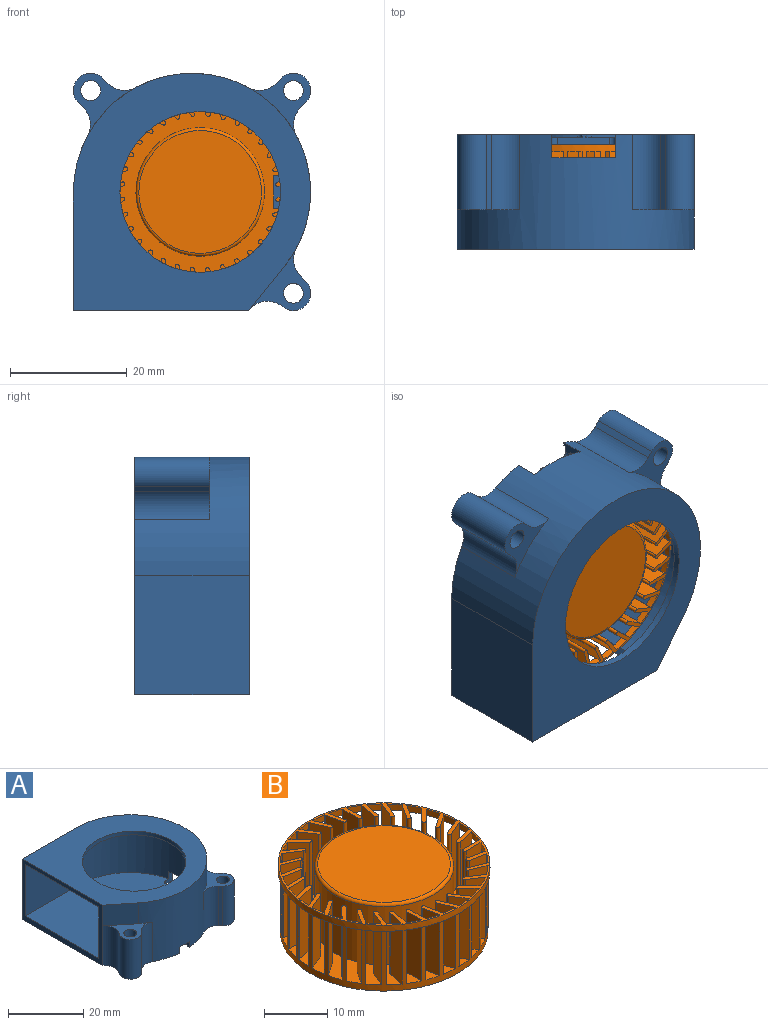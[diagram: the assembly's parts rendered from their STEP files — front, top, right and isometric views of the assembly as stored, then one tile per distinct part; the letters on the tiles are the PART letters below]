
ASSEMBLY  parts=2 mates=1
PART A: 84 faces, bbox 40.6x40.6x19.6 mm
  f0: plane 11x2.45mm, normal (0,0,-1), area 13.4mm2, adj f27,f38,f64,f73
  f1: cylinder r=1mm len=0.99mm, axis (0,0,1), area 0.7mm2, adj f21,f30,f45,f76
  f2: cylinder r=1mm len=0.99mm, axis (0,0,1), area 0.7mm2, adj f7,f15,f26,f76
  f3: cylinder r=1mm len=0.78mm, axis (0,0,-1), area 0.5mm2, adj f24,f76,f81,f82
  f4: cylinder r=1mm len=1mm, axis (0,0,-1), area 0.8mm2, adj f24,f25,f76,f82
  f5: cylinder r=4mm len=12.85mm, axis (0,0,1), area 81.4mm2, adj f53,f56,f75,f76
  f6: plane 8.79x0.5mm, normal (1,0,0), area 4.4mm2, adj f26,f35,f63,f76
  f7: plane 5.11x0.5mm, normal (0,1,0), area 2.6mm2, adj f2,f26,f42,f76
  f8: cylinder r=1mm len=0.99mm, axis (0,0,1), area 0.7mm2, adj f25,f76,f79,f82
  f9: cylinder r=1mm len=0.99mm, axis (0,0,1), area 0.7mm2, adj f43,f47,f51,f76
  f10: cylinder r=1mm len=1mm, axis (0,0,-1), area 0.8mm2, adj f43,f44,f47,f76
  f11: cylinder r=4mm len=12.85mm, axis (0,0,1), area 65.8mm2, adj f17,f48,f73,f76
  f12: cylinder r=4mm len=12.85mm, axis (0,0,1), area 65.8mm2, adj f18,f48,f73,f76
  f13: plane 6.34x3.7mm, normal (0,0,-1), area 23.4mm2, adj f39,f40,f41,f73
  f14: cylinder r=19.75mm len=17.94mm, axis (0,0,1), area 12.7mm2, adj f26,f38,f63,f76
  f15: cylinder r=10.4mm len=9.15mm, axis (0,0,1), area 7mm2, adj f2,f26,f35,f76
  f16: cylinder r=2.95mm len=12.85mm, axis (0,0,1), area 119.1mm2, adj f17,f18,f48,f76
  f17: plane 12.85x0.89mm, normal (0.71,-0.71,0), area 16.1mm2, adj f11,f16,f48,f76
  f18: plane 12.85x0.89mm, normal (-0.71,0.71,0), area 16.1mm2, adj f12,f16,f48,f76
  f19: cylinder r=1.7mm len=12.85mm, axis (0,0,1), area 137.3mm2, adj f48,f76
  f20: plane 18.45x13.51mm, normal (0,0,-1), area 46.2mm2, adj f27,f31,f32,f39,f46,f58,f59,f60
  f21: cylinder r=10.4mm len=8.51mm, axis (0,0,1), area 5.6mm2, adj f1,f22,f30,f76
  f22: plane 3.51x1.7mm, normal (-1,0,0), area 4.5mm2, adj f21,f30,f40,f52,f76,f80
  f23: plane 3.5x1.7mm, normal (1,0,0), area 4.5mm2, adj f40,f52,f76,f79,f80,f82
  f24: plane 6.24x0.5mm, normal (1,0,0), area 3.1mm2, adj f3,f4,f76,f82
  f25: plane 7.55x0.5mm, normal (0,-1,0), area 3.8mm2, adj f4,f8,f76,f82
  f26: plane 20.81x19.01mm, normal (0,0,-1), area 225.9mm2, adj f2,f6,f7,f14,f15,f28,f35,f38
  f27: plane 4x1.7mm, normal (0,1,0), area 5.3mm2, adj f0,f20,f29,f30,f46,f52,f64,f73
  f28: cylinder r=1mm len=1.2mm, axis (0,0,-1), area 1.9mm2, adj f26,f38,f42,f52
  f29: cylinder r=1mm len=1.2mm, axis (0,0,-1), area 1.9mm2, adj f27,f30,f42,f52
  f30: plane 17.97x16.7mm, normal (0,0,-1), area 157.2mm2, adj f1,f21,f22,f27,f29,f39,f40,f42
  f31: cylinder r=4mm len=12.85mm, axis (0,0,1), area 65.8mm2, adj f20,f57,f61,f73
  f32: cylinder r=4mm len=12.85mm, axis (0,0,1), area 65.8mm2, adj f20,f57,f59,f73
  f33: cylinder r=4mm len=12.85mm, axis (0,0,1), area 65.8mm2, adj f53,f55,f73,f76
  f34: cylinder r=1mm len=0.99mm, axis (0,0,1), area 0.7mm2, adj f47,f50,f51,f76
  f35: cylinder r=1mm len=0.99mm, axis (0,0,1), area 0.7mm2, adj f6,f15,f26,f76
  f36: cylinder r=1mm len=1mm, axis (0,0,-1), area 0.8mm2, adj f47,f49,f50,f76
  f37: cylinder r=1mm len=1mm, axis (0,0,-1), area 0.8mm2, adj f44,f47,f49,f76
  f38: plane 4x2.43mm, normal (0,-1,0), area 6mm2, adj f0,f14,f26,f28,f52,f64,f73,f76
  f39: plane 6.26x2mm, normal (-1,0,0), area 9.7mm2, adj f13,f20,f30,f40,f46,f73
  f40: plane 7.53x2.7mm, normal (0,1,0), area 11.9mm2, adj f13,f22,f23,f30,f39,f41,f52,f67
  f41: plane 6.26x2mm, normal (1,0,0), area 9.7mm2, adj f13,f40,f73,f76,f82,f83
  f42: plane 9x1.7mm, normal (1,0,0), area 11.1mm2, adj f7,f26,f28,f29,f30,f45,f52,f76
  f43: plane 7.55x0.5mm, normal (0,1,0), area 3.8mm2, adj f9,f10,f47,f76
  f44: plane 18.85x0.5mm, normal (1,0,0), area 9.4mm2, adj f10,f37,f47,f76
  f45: plane 5.11x0.5mm, normal (0,-1,0), area 2.6mm2, adj f1,f30,f42,f76
  f46: cylinder r=19.75mm len=16.7mm, axis (0,0,1), area 11.1mm2, adj f20,f27,f30,f39
  f47: plane 20.85x19.58mm, normal (0,0,-1), area 328.2mm2, adj f9,f10,f34,f36,f37,f43,f44,f49
  f48: plane 10.65x10.65mm, normal (0,0,1), area 33.8mm2, adj f11,f12,f16,f17,f18,f19,f73
  f49: plane 17.55x0.5mm, normal (0,-1,0), area 8.8mm2, adj f36,f37,f47,f76
  f50: plane 8.83x0.5mm, normal (-1,0,0), area 4.4mm2, adj f34,f36,f47,f76
  f51: cylinder r=10.4mm len=9.15mm, axis (0,0,1), area 7mm2, adj f9,f34,f47,f76
  f52: plane 38.95x37.99mm, normal (0,0,1), area 1185mm2, adj f22,f23,f27,f28,f29,f38,f40,f42
  f53: plane 10.65x10.5mm, normal (0,0,1), area 35.1mm2, adj f5,f33,f54,f55,f56,f73,f75
  f54: cylinder r=1.7mm len=12.85mm, axis (0,0,1), area 137.3mm2, adj f53,f76
  f55: plane 12.85x0.89mm, normal (0.71,-0.71,0), area 16.1mm2, adj f33,f53,f56,f76
  f56: cylinder r=2.95mm len=12.85mm, axis (0,0,1), area 115.5mm2, adj f5,f53,f55,f76
  f57: plane 10.65x10.65mm, normal (0,0,1), area 33.8mm2, adj f31,f32,f58,f59,f60,f61,f73
  f58: cylinder r=1.7mm len=12.85mm, axis (0,0,1), area 137.3mm2, adj f20,f57
  f59: plane 12.85x0.89mm, normal (0.71,0.71,0), area 16.1mm2, adj f20,f32,f57,f60
  f60: cylinder r=2.95mm len=12.85mm, axis (0,0,1), area 119.1mm2, adj f20,f57,f59,f61
  f61: plane 12.85x0.89mm, normal (-0.71,-0.71,0), area 16.1mm2, adj f20,f31,f57,f60
  f62: plane 30x19.6mm, normal (-1,0,0), area 128.5mm2, adj f52,f65,f66,f70,f72,f74,f75,f76
  f63: cylinder r=1mm len=1.07mm, axis (0,0,1), area 0.8mm2, adj f6,f14,f26,f76
  f64: cylinder r=19.1mm len=38.2mm, axis (0,0,1), area 1342mm2, adj f0,f27,f38,f52,f65,f66,f67,f68
  f65: plane 16.7x2.67mm, normal (-0.38,0.92,0), area 48.3mm2, adj f52,f62,f64,f70
  f66: plane 20.42x16.7mm, normal (0,-1,0), area 341.1mm2, adj f52,f62,f64,f70
  f67: plane 5.62x5.14mm, normal (0,0,1), area 28.5mm2, adj f40,f64,f68,f69
  f68: plane 4.93x1.5mm, normal (1,0,0), area 7.4mm2, adj f40,f52,f64,f67
  f69: plane 4.94x1.5mm, normal (-1,0,0), area 7.4mm2, adj f40,f52,f64,f67
  f70: plane 39.42x38.2mm, normal (0,0,-1), area 667.8mm2, adj f62,f64,f65,f66,f71
  f71: cylinder r=13.75mm len=27.5mm, axis (0,0,-1), area 103.7mm2, adj f70,f72
  f72: plane 40.62x40.6mm, normal (0,0,1), area 803.1mm2, adj f62,f71,f73,f74,f75
  f73: cylinder r=20.3mm len=40.6mm, axis (0,0,1), area 1117.4mm2, adj f0,f11,f12,f13,f20,f27,f31,f32
  f74: plane 20.32x19.6mm, normal (0,1,0), area 398.3mm2, adj f62,f72,f73,f76
  f75: plane 19.6x7.59mm, normal (-0.63,-0.78,0), area 67.8mm2, adj f5,f53,f62,f72,f73,f76
  f76: plane 40.62x40.6mm, normal (0,0,-1), area 170.7mm2, adj f1,f2,f3,f4,f5,f6,f7,f8
  f77: plane 19.6x19.6mm, normal (0,0,-1), area 301.7mm2, adj f78
  f78: cylinder r=9.8mm len=19.6mm, axis (0,0,1), area 30.8mm2, adj f76,f77
  f79: cylinder r=10.4mm len=8.51mm, axis (0,0,1), area 5.7mm2, adj f8,f23,f76,f82
  f80: cylinder r=9.8mm len=7.53mm, axis (0,0,1), area 13.1mm2, adj f22,f23,f52,f76
  f81: plane 7.12x5.66mm, normal (0.62,0.78,0), area 4.5mm2, adj f3,f76,f82,f83
  f82: plane 18.04x17.97mm, normal (0,0,-1), area 184.8mm2, adj f3,f4,f8,f23,f24,f25,f40,f41
  f83: cylinder r=19.75mm len=10.54mm, axis (0,0,1), area 5.8mm2, adj f41,f76,f81,f82
PART B: 169 faces, bbox 33.5x33.5x13 mm
  f0: cylinder r=16.45mm len=2.21mm, axis (0,0,-1), area 3mm2, adj f6,f11,f64,f168
  f1: cylinder r=0.34mm len=11.8mm, axis (0,0,1), area 1.6mm2, adj f69,f99,f152,f156,f168
  f2: plane 11.8x2.48mm, normal (-0.7,-0.72,0), area 40.8mm2, adj f89,f152,f153,f168
  f3: plane 11.8x3.38mm, normal (0.98,0.21,0), area 40.8mm2, adj f59,f106,f152,f168
  f4: plane 11.8x3.23mm, normal (-0.98,-0.21,0), area 39mm2, adj f28,f106,f152,f156,f168
  f5: plane 11.8x3.46mm, normal (1,0.01,0), area 40.8mm2, adj f7,f85,f152,f168
  f6: plane 11.8x3.3mm, normal (-1,-0.01,0), area 39mm2, adj f0,f85,f152,f156,f168
  f7: cylinder r=0.34mm len=11.8mm, axis (0,0,1), area 1.6mm2, adj f5,f28,f152,f156,f168
  f8: plane 11.8x3.4mm, normal (0.98,-0.18,0), area 40.8mm2, adj f9,f11,f152,f168
  f9: cylinder r=0.34mm len=11.8mm, axis (0,0,1), area 12.8mm2, adj f8,f10,f152,f168
  f10: plane 11.8x3.25mm, normal (-0.98,0.18,0), area 39mm2, adj f9,f44,f152,f156,f168
  f11: cylinder r=0.34mm len=11.8mm, axis (0,0,1), area 1.6mm2, adj f0,f8,f152,f156,f168
  f12: plane 11.8x3.21mm, normal (0.93,-0.37,0), area 40.8mm2, adj f13,f15,f152,f168
  f13: cylinder r=0.34mm len=11.8mm, axis (0,0,1), area 12.8mm2, adj f12,f14,f152,f168
  f14: plane 11.8x3.07mm, normal (-0.93,0.37,0), area 39mm2, adj f13,f105,f152,f156,f168
  f15: cylinder r=0.34mm len=11.8mm, axis (0,0,1), area 1.6mm2, adj f12,f44,f152,f156,f168
  f16: plane 11.8x2.9mm, normal (0.84,-0.54,0), area 40.8mm2, adj f17,f19,f152,f168
  f17: cylinder r=0.34mm len=11.8mm, axis (0,0,1), area 12.8mm2, adj f16,f18,f152,f168
  f18: plane 11.8x2.77mm, normal (-0.84,0.54,0), area 39mm2, adj f17,f104,f152,f156,f168
  f19: cylinder r=0.34mm len=11.8mm, axis (0,0,1), area 1.6mm2, adj f16,f105,f152,f156,f168
  f20: plane 11.8x2.48mm, normal (0.72,-0.7,0), area 40.8mm2, adj f21,f23,f152,f168
  f21: cylinder r=0.34mm len=11.8mm, axis (0,0,1), area 12.8mm2, adj f20,f22,f152,f168
  f22: plane 11.8x2.37mm, normal (-0.72,0.7,0), area 39mm2, adj f21,f103,f152,f156,f168
  f23: cylinder r=0.34mm len=11.8mm, axis (0,0,1), area 1.6mm2, adj f20,f104,f152,f156,f168
  f24: plane 11.8x2.85mm, normal (0.57,-0.82,0), area 40.8mm2, adj f72,f109,f152,f168
  f25: cylinder r=16.45mm len=1.94mm, axis (0,0,-1), area 3mm2, adj f64,f122,f149,f168
  f26: cylinder r=16.45mm len=2.21mm, axis (0,0,-1), area 3mm2, adj f64,f113,f123,f168
  f27: cylinder r=16.45mm len=2.4mm, axis (0,0,-1), area 3mm2, adj f60,f64,f125,f168
  f28: cylinder r=16.45mm len=2.4mm, axis (0,0,-1), area 3mm2, adj f4,f7,f64,f168
  f29: cylinder r=16.45mm len=2.49mm, axis (0,0,-1), area 3mm2, adj f45,f59,f64,f168
  f30: cylinder r=16.45mm len=2.49mm, axis (0,0,-1), area 3mm2, adj f43,f64,f140,f168
  f31: cylinder r=16.45mm len=2.4mm, axis (0,0,-1), area 3mm2, adj f50,f64,f141,f168
  f32: cylinder r=16.45mm len=2.21mm, axis (0,0,-1), area 3mm2, adj f64,f135,f138,f168
  f33: cylinder r=16.45mm len=1.94mm, axis (0,0,-1), area 3mm2, adj f64,f68,f136,f168
  f34: cylinder r=16.45mm len=1.94mm, axis (0,0,-1), area 3mm2, adj f64,f74,f93,f168
  f35: cylinder r=16.45mm len=2.21mm, axis (0,0,-1), area 3mm2, adj f64,f66,f115,f168
  f36: cylinder r=16.45mm len=2.4mm, axis (0,0,-1), area 3mm2, adj f64,f107,f131,f168
  f37: cylinder r=16.45mm len=2.49mm, axis (0,0,-1), area 3mm2, adj f64,f114,f130,f168
  f38: plane 32.9x32.9mm, normal (0,0,-1), area 849.9mm2, adj f156
  f39: cylinder r=16.45mm len=2.49mm, axis (0,0,-1), area 3mm2, adj f56,f64,f127,f168
  f40: cylinder r=16.45mm len=2.49mm, axis (0,0,-1), area 3mm2, adj f64,f83,f84,f168
  f41: cylinder r=0.34mm len=11.8mm, axis (0,0,1), area 12.8mm2, adj f149,f152,f159,f168
  f42: cylinder r=0.34mm len=11.8mm, axis (0,0,1), area 12.8mm2, adj f60,f61,f152,f168
  f43: cylinder r=0.34mm len=11.8mm, axis (0,0,1), area 1.6mm2, adj f30,f58,f152,f156,f168
  f44: cylinder r=16.45mm len=1.94mm, axis (0,0,-1), area 3mm2, adj f10,f15,f64,f168
  f45: plane 11.8x3.04mm, normal (-0.92,-0.4,0), area 39mm2, adj f29,f82,f152,f156,f168
  f46: cylinder r=0.34mm len=11.8mm, axis (0,0,1), area 1.6mm2, adj f142,f152,f156,f162,f168
  f47: plane 11.8x3.46mm, normal (0.01,-1,0), area 40.8mm2, adj f48,f150,f152,f168
  f48: cylinder r=0.34mm len=11.8mm, axis (0,0,1), area 12.8mm2, adj f47,f151,f152,f168
  f49: cylinder r=0.34mm len=11.8mm, axis (0,0,1), area 12.8mm2, adj f69,f147,f152,f168
  f50: plane 11.8x2.37mm, normal (-0.7,-0.72,0), area 39mm2, adj f31,f57,f152,f156,f168
  f51: cylinder r=0.34mm len=11.8mm, axis (0,0,1), area 1.6mm2, adj f86,f98,f152,f156,f168
  f52: cylinder r=0.34mm len=11.8mm, axis (0,0,1), area 12.8mm2, adj f143,f152,f157,f168
  f53: cylinder r=0.34mm len=11.8mm, axis (0,0,1), area 12.8mm2, adj f66,f116,f152,f168
  f54: cylinder r=0.34mm len=11.8mm, axis (0,0,1), area 1.6mm2, adj f81,f152,f156,f163,f168
  f55: cylinder r=0.34mm len=11.8mm, axis (0,0,1), area 12.8mm2, adj f56,f124,f152,f168
  f56: plane 11.8x2.72mm, normal (0.57,-0.82,0), area 39mm2, adj f39,f55,f152,f156,f168
  f57: cylinder r=0.34mm len=11.8mm, axis (0,0,1), area 12.8mm2, adj f50,f137,f152,f168
  f58: plane 11.8x3.18mm, normal (0.92,0.4,0), area 40.8mm2, adj f43,f82,f152,f168
  f59: cylinder r=0.34mm len=11.8mm, axis (0,0,1), area 1.6mm2, adj f3,f29,f152,f156,f168
  f60: plane 11.8x2.37mm, normal (0.72,-0.7,0), area 39mm2, adj f27,f42,f152,f156,f168
  f61: plane 11.8x2.48mm, normal (-0.72,0.7,0), area 40.8mm2, adj f42,f123,f152,f168
  f62: plane 11.8x3.04mm, normal (-0.4,0.92,0), area 39mm2, adj f70,f152,f156,f162,f168
  f63: cylinder r=0.34mm len=11.8mm, axis (0,0,1), area 12.8mm2, adj f76,f86,f152,f168
  f64: plane 33.55x33.55mm, normal (0,0,-1), area 34mm2, adj f0,f25,f26,f27,f28,f29,f30,f31
  f65: cylinder r=0.34mm len=11.8mm, axis (0,0,1), area 12.8mm2, adj f81,f84,f152,f168
  f66: plane 11.8x3.3mm, normal (0.01,-1,0), area 39mm2, adj f35,f53,f152,f156,f168
  f67: plane 11.8x3.18mm, normal (0.4,-0.92,0), area 40.8mm2, adj f70,f87,f152,f168
  f68: plane 11.8x3.07mm, normal (-0.37,-0.93,0), area 39mm2, adj f33,f75,f152,f156,f168
  f69: plane 11.8x3.4mm, normal (-0.18,-0.98,0), area 40.8mm2, adj f1,f49,f152,f168
  f70: cylinder r=0.34mm len=11.8mm, axis (0,0,1), area 12.8mm2, adj f62,f67,f152,f168
  f71: cylinder r=0.34mm len=11.8mm, axis (0,0,1), area 1.6mm2, adj f92,f152,f156,f161,f168
  f72: cylinder r=0.34mm len=11.8mm, axis (0,0,1), area 12.8mm2, adj f24,f152,f158,f168
  f73: cylinder r=0.34mm len=11.8mm, axis (0,0,1), area 12.8mm2, adj f119,f152,f167,f168
  f74: plane 11.8x3.25mm, normal (-0.18,-0.98,0), area 39mm2, adj f34,f148,f152,f156,f168
  f75: cylinder r=0.34mm len=11.8mm, axis (0,0,1), area 12.8mm2, adj f68,f133,f152,f168
  f76: plane 11.8x3.07mm, normal (0.37,0.93,0), area 39mm2, adj f63,f96,f152,f156,f168
  f77: plane 11.8x3.23mm, normal (-0.21,0.98,0), area 39mm2, adj f100,f152,f156,f160,f168
  f78: cylinder r=0.34mm len=11.8mm, axis (0,0,1), area 1.6mm2, adj f143,f152,f156,f164,f168
  f79: plane 11.8x3.18mm, normal (-0.4,0.92,0), area 40.8mm2, adj f126,f127,f152,f168
  f80: cylinder r=0.34mm len=11.8mm, axis (0,0,1), area 1.6mm2, adj f144,f152,f155,f156,f168
  f81: plane 11.8x3.18mm, normal (-0.92,-0.4,0), area 40.8mm2, adj f54,f65,f152,f168
  f82: cylinder r=0.34mm len=11.8mm, axis (0,0,1), area 12.8mm2, adj f45,f58,f152,f168
  f83: cylinder r=0.34mm len=11.8mm, axis (0,0,1), area 1.6mm2, adj f40,f110,f152,f156,f168
  f84: plane 11.8x3.04mm, normal (0.92,0.4,0), area 39mm2, adj f40,f65,f152,f156,f168
  f85: cylinder r=0.34mm len=11.8mm, axis (0,0,1), area 12.8mm2, adj f5,f6,f152,f168
  f86: plane 11.8x3.21mm, normal (-0.37,-0.93,0), area 40.8mm2, adj f51,f63,f152,f168
  f87: cylinder r=0.34mm len=11.8mm, axis (0,0,1), area 1.6mm2, adj f67,f152,f156,f166,f168
  f88: cylinder r=11mm len=22mm, axis (0,0,1), area 781mm2, adj f101,f152
  f89: cylinder r=0.34mm len=11.8mm, axis (0,0,1), area 12.8mm2, adj f2,f117,f152,f168
  f90: cylinder r=0.34mm len=11.8mm, axis (0,0,1), area 12.8mm2, adj f112,f144,f152,f168
  f91: cylinder r=0.34mm len=11.8mm, axis (0,0,1), area 1.6mm2, adj f152,f156,f159,f165,f168
  f92: plane 11.8x2.85mm, normal (-0.82,-0.57,0), area 40.8mm2, adj f71,f120,f152,f168
  f93: cylinder r=0.34mm len=11.8mm, axis (0,0,1), area 1.6mm2, adj f34,f133,f152,f156,f168
  f94: plane 11.8x2.9mm, normal (0.54,0.84,0), area 40.8mm2, adj f134,f136,f152,f168
  f95: cylinder r=0.34mm len=11.8mm, axis (0,0,1), area 1.6mm2, adj f96,f152,f156,f167,f168
  f96: cylinder r=16.45mm len=1.94mm, axis (0,0,-1), area 3mm2, adj f64,f76,f95,f168
  f97: cylinder r=16.45mm len=2.21mm, axis (0,0,-1), area 3mm2, adj f64,f119,f153,f168
  f98: cylinder r=16.45mm len=1.94mm, axis (0,0,-1), area 3mm2, adj f51,f64,f147,f168
  f99: cylinder r=16.45mm len=2.21mm, axis (0,0,-1), area 3mm2, adj f1,f64,f151,f168
  f100: cylinder r=16.45mm len=2.4mm, axis (0,0,-1), area 3mm2, adj f64,f77,f150,f168
  f101: torus R=10.5mm, axis (0,0,1), area 53.4mm2, adj f88,f102
  f102: plane 21x21mm, normal (0,0,1), area 346.4mm2, adj f101
  f103: cylinder r=16.45mm len=2.4mm, axis (0,0,-1), area 3mm2, adj f22,f64,f109,f168
  f104: cylinder r=16.45mm len=2.21mm, axis (0,0,-1), area 3mm2, adj f18,f23,f64,f168
  f105: cylinder r=16.45mm len=1.94mm, axis (0,0,-1), area 3mm2, adj f14,f19,f64,f168
  f106: cylinder r=0.34mm len=11.8mm, axis (0,0,1), area 12.8mm2, adj f3,f4,f152,f168
  f107: plane 11.8x3.23mm, normal (0.21,-0.98,0), area 39mm2, adj f36,f129,f152,f156,f168
  f108: cylinder r=16.77mm len=33.55mm, axis (0,0,-1), area 126.5mm2, adj f64,f168
  f109: cylinder r=0.34mm len=11.8mm, axis (0,0,1), area 1.6mm2, adj f24,f103,f152,f156,f168
  f110: plane 11.8x3.38mm, normal (-0.98,-0.21,0), area 40.8mm2, adj f83,f146,f152,f168
  f111: plane 11.8x3.23mm, normal (0.98,0.21,0), area 39mm2, adj f146,f152,f155,f156,f168
  f112: plane 11.8x3.3mm, normal (1,0.01,0), area 39mm2, adj f90,f152,f156,f164,f168
  f113: plane 11.8x2.77mm, normal (0.84,-0.54,0), area 39mm2, adj f26,f145,f152,f156,f168
  f114: plane 11.8x3.04mm, normal (0.4,-0.92,0), area 39mm2, adj f37,f126,f152,f156,f168
  f115: cylinder r=0.34mm len=11.8mm, axis (0,0,1), area 1.6mm2, adj f35,f132,f152,f156,f168
  f116: plane 11.8x3.46mm, normal (-0.01,1,0), area 40.8mm2, adj f53,f131,f152,f168
  f117: plane 11.8x2.37mm, normal (0.7,0.72,0), area 39mm2, adj f89,f152,f156,f161,f168
  f118: cylinder r=0.34mm len=11.8mm, axis (0,0,1), area 12.8mm2, adj f139,f140,f152,f168
  f119: plane 11.8x2.77mm, normal (0.54,0.84,0), area 39mm2, adj f73,f97,f152,f156,f168
  f120: cylinder r=0.34mm len=11.8mm, axis (0,0,1), area 12.8mm2, adj f92,f152,f154,f168
  f121: plane 11.8x2.9mm, normal (-0.84,0.54,0), area 40.8mm2, adj f122,f145,f152,f168
  f122: cylinder r=0.34mm len=11.8mm, axis (0,0,1), area 1.6mm2, adj f25,f121,f152,f156,f168
  f123: cylinder r=0.34mm len=11.8mm, axis (0,0,1), area 1.6mm2, adj f26,f61,f152,f156,f168
  f124: plane 11.8x2.85mm, normal (-0.57,0.82,0), area 40.8mm2, adj f55,f125,f152,f168
  f125: cylinder r=0.34mm len=11.8mm, axis (0,0,1), area 1.6mm2, adj f27,f124,f152,f156,f168
  f126: cylinder r=0.34mm len=11.8mm, axis (0,0,1), area 12.8mm2, adj f79,f114,f152,f168
  f127: cylinder r=0.34mm len=11.8mm, axis (0,0,1), area 1.6mm2, adj f39,f79,f152,f156,f168
  f128: plane 11.8x3.38mm, normal (-0.21,0.98,0), area 40.8mm2, adj f129,f130,f152,f168
  f129: cylinder r=0.34mm len=11.8mm, axis (0,0,1), area 12.8mm2, adj f107,f128,f152,f168
  f130: cylinder r=0.34mm len=11.8mm, axis (0,0,1), area 1.6mm2, adj f37,f128,f152,f156,f168
  f131: cylinder r=0.34mm len=11.8mm, axis (0,0,1), area 1.6mm2, adj f36,f116,f152,f156,f168
  f132: plane 11.8x3.4mm, normal (0.18,0.98,0), area 40.8mm2, adj f115,f148,f152,f168
  f133: plane 11.8x3.21mm, normal (0.37,0.93,0), area 40.8mm2, adj f75,f93,f152,f168
  f134: cylinder r=0.34mm len=11.8mm, axis (0,0,1), area 12.8mm2, adj f94,f135,f152,f168
  f135: plane 11.8x2.77mm, normal (-0.54,-0.84,0), area 39mm2, adj f32,f134,f152,f156,f168
  f136: cylinder r=0.34mm len=11.8mm, axis (0,0,1), area 1.6mm2, adj f33,f94,f152,f156,f168
  f137: plane 11.8x2.48mm, normal (0.7,0.72,0), area 40.8mm2, adj f57,f138,f152,f168
  f138: cylinder r=0.34mm len=11.8mm, axis (0,0,1), area 1.6mm2, adj f32,f137,f152,f156,f168
  f139: plane 11.8x2.85mm, normal (0.82,0.57,0), area 40.8mm2, adj f118,f141,f152,f168
  f140: plane 11.8x2.72mm, normal (-0.82,-0.57,0), area 39mm2, adj f30,f118,f152,f156,f168
  f141: cylinder r=0.34mm len=11.8mm, axis (0,0,1), area 1.6mm2, adj f31,f139,f152,f156,f168
  f142: plane 11.8x3.38mm, normal (0.21,-0.98,0), area 40.8mm2, adj f46,f152,f160,f168
  f143: plane 11.8x3.4mm, normal (-0.98,0.18,0), area 40.8mm2, adj f52,f78,f152,f168
  f144: plane 11.8x3.46mm, normal (-1,-0.01,0), area 40.8mm2, adj f80,f90,f152,f168
  f145: cylinder r=0.34mm len=11.8mm, axis (0,0,1), area 12.8mm2, adj f113,f121,f152,f168
  f146: cylinder r=0.34mm len=11.8mm, axis (0,0,1), area 12.8mm2, adj f110,f111,f152,f168
  f147: plane 11.8x3.25mm, normal (0.18,0.98,0), area 39mm2, adj f49,f98,f152,f156,f168
  f148: cylinder r=0.34mm len=11.8mm, axis (0,0,1), area 12.8mm2, adj f74,f132,f152,f168
  f149: plane 11.8x3.07mm, normal (0.93,-0.37,0), area 39mm2, adj f25,f41,f152,f156,f168
  f150: cylinder r=0.34mm len=11.8mm, axis (0,0,1), area 1.6mm2, adj f47,f100,f152,f156,f168
  f151: plane 11.8x3.3mm, normal (-0.01,1,0), area 39mm2, adj f48,f99,f152,f156,f168
  f152: plane 32.89x32.89mm, normal (0,0,1), area 387.7mm2, adj f1,f2,f3,f4,f5,f6,f7,f8
  f153: cylinder r=0.34mm len=11.8mm, axis (0,0,1), area 1.6mm2, adj f2,f97,f152,f156,f168
  f154: plane 11.8x2.72mm, normal (0.82,0.57,0), area 39mm2, adj f120,f152,f156,f163,f168
  f155: cylinder r=16.45mm len=2.4mm, axis (0,0,-1), area 3mm2, adj f64,f80,f111,f168
  f156: cylinder r=16.45mm len=32.9mm, axis (0,0,1), area 368.4mm2, adj f1,f4,f6,f7,f10,f11,f14,f15
  f157: plane 11.8x3.25mm, normal (0.98,-0.18,0), area 39mm2, adj f52,f152,f156,f165,f168
  f158: plane 11.8x2.72mm, normal (-0.57,0.82,0), area 39mm2, adj f72,f152,f156,f166,f168
  f159: plane 11.8x3.21mm, normal (-0.93,0.37,0), area 40.8mm2, adj f41,f91,f152,f168
  f160: cylinder r=0.34mm len=11.8mm, axis (0,0,1), area 12.8mm2, adj f77,f142,f152,f168
  f161: cylinder r=16.45mm len=2.4mm, axis (0,0,-1), area 3mm2, adj f64,f71,f117,f168
  f162: cylinder r=16.45mm len=2.49mm, axis (0,0,-1), area 3mm2, adj f46,f62,f64,f168
  f163: cylinder r=16.45mm len=2.49mm, axis (0,0,-1), area 3mm2, adj f54,f64,f154,f168
  f164: cylinder r=16.45mm len=2.21mm, axis (0,0,-1), area 3mm2, adj f64,f78,f112,f168
  f165: cylinder r=16.45mm len=1.94mm, axis (0,0,-1), area 3mm2, adj f64,f91,f157,f168
  f166: cylinder r=16.45mm len=2.49mm, axis (0,0,-1), area 3mm2, adj f64,f87,f158,f168
  f167: plane 11.8x2.9mm, normal (-0.54,-0.84,0), area 40.8mm2, adj f73,f95,f152,f168
  f168: plane 33.55x33.55mm, normal (0,0,1), area 116mm2, adj f0,f1,f2,f3,f4,f5,f6,f7
PLACE A rot(axis=(0.58,-0.58,0.58),120deg) t=(-37,-1.1,-13.96)mm
PLACE B rot(axis=(0.58,-0.58,0.58),120deg) t=(-37,1.4,-13.96)mm
MATE fastened B.f88 <-> A.f15  axis (0,1,0) through (-37,-2.8,-13.96)mm
